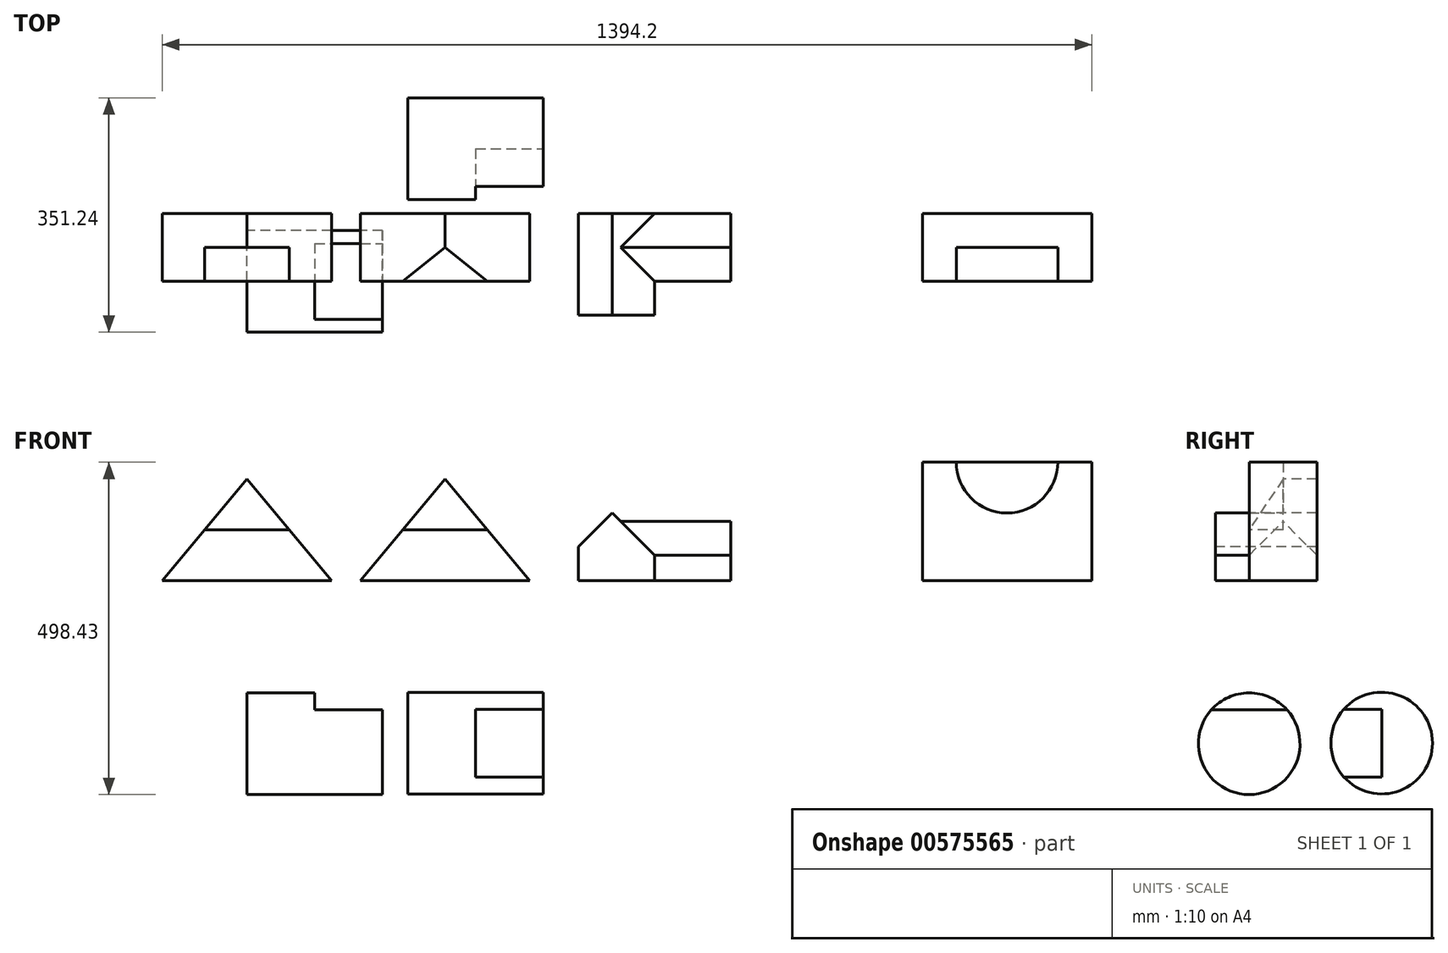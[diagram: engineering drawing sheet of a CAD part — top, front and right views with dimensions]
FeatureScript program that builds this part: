
annotation { "Feature Type Name" : "Feature", "Feature Type Description" : "" }
export const myFeature = defineFeature(function(context is Context, id is Id, definition is map)
    precondition{}
    {
        {
            var Q0;
            Q0=qCreatedBy(makeId("Front.planeOp"),FACE);
            var sketch = newSketch(context, id + "F0", { "sketchPlane" : qUnion([Q0])});
            skLineSegment(sketch, "E0", {"start": v(0, 0) * mm, "end": v(-127, 0) * mm});
            skLineSegment(sketch, "E1", {"start": v(-127, 0) * mm, "end": v(0, 152.4) * mm});
            skLineSegment(sketch, "E2", {"start": v(0, 0) * mm, "end": v(127, 0) * mm});
            skLineSegment(sketch, "E3", {"start": v(127, 0) * mm, "end": v(0, 152.4) * mm});
            skLineSegment(sketch, "E4", {"start": v(0, 76.2) * mm, "end": v(-63.5, 76.2) * mm});
            skLineSegment(sketch, "E5", {"start": v(0, 76.2) * mm, "end": v(63.5, 76.2) * mm});
            skSolve(sketch);
        }
        {
            var Q0;
            {var subQ3=sQuery(id+"F0.wireOp",EDGE,"E4");Q0=makeQuery(id+"F0.imprint","IMPRINT",FACE,{"disambiguationData":[TD([[makeQuery(id+"F0.imprint","IMPRINT",EDGE,{"derivedFrom":subQ3}),-1.0]])]});}
            var Q1;
            {var subQ4=sQuery(id+"F0.wireOp",EDGE,"E0");Q1=makeQuery(id+"F0.imprint","IMPRINT",FACE,{"disambiguationData":[TD([[makeQuery(id+"F0.imprint","IMPRINT",EDGE,{"derivedFrom":subQ4}),-1.0]])]});}
            extrude(context, id + "F1", {"entities" : qUnion([Q0, Q1]), "oppositeDirection" : true, "depth" : 101.6 * mm, "offsetDistance" : 25.4 * mm});
        }
        {
            var Q0;
            Q0=makeQuery(id+"F1.opExtrude","CAP_FACE",FACE,{"disambiguationData":[OSD([sQuery(id+"F0.wireOp",EDGE,"E0"),sQuery(id+"F0.wireOp",EDGE,"E1"),sQuery(id+"F0.wireOp",EDGE,"E2"),sQuery(id+"F0.wireOp",EDGE,"E3")])],"isStart":true});
            var sketch = newSketch(context, id + "F2", { "sketchPlane" : qUnion([Q0])});
            skLineSegment(sketch, "E6", {"start": v(0, 76.2) * mm, "end": v(-63.5, 76.2) * mm});
            skLineSegment(sketch, "E7", {"start": v(0, 76.2) * mm, "end": v(63.5, 76.2) * mm});
            skSolve(sketch);
        }
        {
            var Q0;
            {var subQ0=sQuery(id+"F2.wireOp",EDGE,"E6");Q0=makeQuery(id+"F2.imprint","IMPRINT",FACE,{"disambiguationData":[TD([[makeQuery(id+"F2.imprint","IMPRINT",EDGE,{"derivedFrom":subQ0}),-1.0]])]});}
            extrude(context, id + "F3", {"entities" : qUnion([Q0]), "operationType" : NewBodyOperationType.REMOVE, "oppositeDirection" : true, "depth" : 50.8 * mm, "offsetDistance" : 25.4 * mm});
        }
        {
            var Q0;
            Q0=qCreatedBy(makeId("Front.planeOp"),FACE);
            var sketch = newSketch(context, id + "F4", { "sketchPlane" : qUnion([Q0])});
            skLineSegment(sketch, "E8", {"start": v(170.18, 0) * mm, "end": v(424.18, 0) * mm});
            skLineSegment(sketch, "E9", {"start": v(297.18, 152.4) * mm, "end": v(170.18, 0) * mm});
            skLineSegment(sketch, "E10", {"start": v(297.18, 152.4) * mm, "end": v(424.18, 0) * mm});
            skLineSegment(sketch, "E11", {"start": v(297.18, 76.2) * mm, "end": v(233.68, 76.2) * mm});
            skLineSegment(sketch, "E12", {"start": v(297.18, 76.2) * mm, "end": v(360.68, 76.2) * mm});
            skSolve(sketch);
        }
        {
            var Q0;
            Q0 = qSketchRegion(id + "F4", true);
            extrude(context, id + "F5", {"entities" : qUnion([Q0]), "oppositeDirection" : true, "depth" : 101.6 * mm, "offsetDistance" : 25.4 * mm});
        }
        {
            var Q0;
            Q0=qCreatedBy(makeId("Front.planeOp"),FACE);
            var sketch = newSketch(context, id + "F6", { "sketchPlane" : qUnion([Q0])});
            skLineSegment(sketch, "E13", {"start": v(497, 0) * mm, "end": v(598.6, 0) * mm});
            skLineSegment(sketch, "E14", {"start": v(598.6, 0) * mm, "end": v(598.6, 50.8) * mm});
            skLineSegment(sketch, "E15", {"start": v(497, 0) * mm, "end": v(497, 50.8) * mm});
            skLineSegment(sketch, "E16", {"start": v(547.8, 101.6) * mm, "end": v(497, 50.8) * mm});
            skLineSegment(sketch, "E17", {"start": v(547.8, 101.6) * mm, "end": v(598.6, 50.8) * mm});
            skLineSegment(sketch, "E18", {"start": v(598.6, 0) * mm, "end": v(725.6, 0) * mm});
            skLineSegment(sketch, "E19", {"start": v(725.6, 0) * mm, "end": v(725.6, 50.8) * mm});
            skLineSegment(sketch, "E20", {"start": v(725.6, 50.8) * mm, "end": v(598.6, 50.8) * mm});
            skLineSegment(sketch, "E21", {"start": v(725.6, 50.8) * mm, "end": v(725.6, 88.9) * mm});
            skLineSegment(sketch, "E22", {"start": v(725.6, 88.9) * mm, "end": v(560.5, 88.9) * mm});
            skSolve(sketch);
        }
        {
            var Q0;
            Q0=makeQuery(id+"F6.imprint","IMPRINT",FACE,{"disambiguationData":[TD([[makeQuery(id+"F6.imprint","IMPRINT",EDGE,{"derivedFrom":sQuery(id+"F6.wireOp",EDGE,"E13")}),1.0]])]});
            var Q1;
            {var subQ0=sQuery(id+"F6.wireOp",EDGE,"E20");Q1=makeQuery(id+"F6.imprint","IMPRINT",FACE,{"disambiguationData":[TD([[makeQuery(id+"F6.imprint","IMPRINT",EDGE,{"derivedFrom":subQ0}),-1.0]])]});}
            var Q2;
            Q2=makeQuery(id+"F6.imprint","IMPRINT",FACE,{"disambiguationData":[TD([[makeQuery(id+"F6.imprint","IMPRINT",EDGE,{"derivedFrom":sQuery(id+"F6.wireOp",EDGE,"E14")}),-1.0]])]});
            extrude(context, id + "F7", {"entities" : qUnion([Q0, Q1, Q2]), "oppositeDirection" : true, "depth" : 101.6 * mm, "offsetDistance" : 25.4 * mm});
        }
        {
            var Q0;
            Q0=makeQuery(id+"F7.opExtrude","CAP_EDGE",EDGE,{"disambiguationData":[OSD([sQuery(id+"F6.wireOp",EDGE,"E22")])],"isStart":true});
            var Q1;
            Q1=makeQuery(id+"F7.opExtrude","CAP_EDGE",EDGE,{"disambiguationData":[OSD([sQuery(id+"F6.wireOp",EDGE,"E22")])],"isStart":false});
            chamfer(context, id + "F8", {"entities" : qUnion([Q0, Q1]), "width" : 50.8 * mm, "tangentPropagation" : true});
        }
        {
            var Q0;
            Q0=qCreatedBy(makeId("Front.planeOp"),FACE);
            var sketch = newSketch(context, id + "F9", { "sketchPlane" : qUnion([Q0])});
            skLineSegment(sketch, "E23", {"start": v(1013.2, 0) * mm, "end": v(1267.2, 0) * mm});
            skLineSegment(sketch, "E24", {"start": v(1267.2, 0) * mm, "end": v(1267.2, 177.8) * mm});
            skLineSegment(sketch, "E25", {"start": v(1267.2, 177.8) * mm, "end": v(1216.4, 177.8) * mm});
            skLineSegment(sketch, "E26", {"start": v(1013.2, 0) * mm, "end": v(1013.2, 177.8) * mm});
            skLineSegment(sketch, "E27", {"start": v(1013.2, 177.8) * mm, "end": v(1064, 177.8) * mm});
            skLineSegment(sketch, "E28", {"start": v(1064, 177.8) * mm, "end": v(1216.4, 177.8) * mm});
            skArc(sketch, "E29", {"start": v(1064, 177.8) * mm, "mid": v(1140.2, 101.6) * mm, "end": v(1216.4, 177.8) * mm});
            skSolve(sketch);
        }
        {
            var Q0;
            Q0=makeQuery(id+"F9.imprint","IMPRINT",FACE,{"disambiguationData":[TD([[makeQuery(id+"F9.imprint","IMPRINT",EDGE,{"derivedFrom":sQuery(id+"F9.wireOp",EDGE,"E23")}),1.0]])]});
            extrude(context, id + "F10", {"entities" : qUnion([Q0]), "oppositeDirection" : true, "depth" : 101.6 * mm, "offsetDistance" : 25.4 * mm});
        }
        {
            var Q0;
            Q0 = qSketchRegion(id + "F9", true);
            extrude(context, id + "F11", {"entities" : qUnion([Q0]), "operationType" : NewBodyOperationType.ADD, "oppositeDirection" : true, "depth" : 101.6 * mm, "offsetDistance" : 25.4 * mm});
        }
        {
            var Q0;
            Q0 = qSketchRegion(id + "F9", true);
            var Q1;
            {var subQ0=sQuery(id+"F9.wireOp",EDGE,"E27");var subQ1=sQuery(id+"F9.wireOp",EDGE,"E26");var subQ2=sQuery(id+"F9.wireOp",EDGE,"E25");var subQ3=sQuery(id+"F9.wireOp",EDGE,"E24");var subQ4=sQuery(id+"F9.wireOp",EDGE,"E23");Q1=makeQuery(id+"F11.boolean.opBoolean","MERGE",FACE,{"derivedFrom":[makeQuery(id+"F10.opExtrude","CAP_FACE",FACE,{"disambiguationData":[OSD([subQ4,subQ3,subQ2,subQ1,subQ0,sQuery(id+"F9.wireOp",EDGE,"E29")])],"isStart":true}),makeQuery(id+"F11.opExtrude","CAP_FACE",FACE,{"disambiguationData":[OSD([subQ4,subQ3,subQ2,subQ1,subQ0,sQuery(id+"F9.wireOp",EDGE,"E28")])],"isStart":true})]});}
            extrude(context, id + "F12", {"entities" : qUnion([Q0, Q1]), "operationType" : NewBodyOperationType.REMOVE, "oppositeDirection" : true, "depth" : 50.8 * mm, "offsetDistance" : 25.4 * mm});
        }
        {
            var Q0;
            Q0=makeQuery(id+"F12.boolean.opBoolean","COPY",FACE,{"derivedFrom":makeQuery(id+"F12.opExtrude","CAP_FACE",FACE,{"disambiguationData":[OSD([sQuery(id+"F9.wireOp",EDGE,"E23"),sQuery(id+"F9.wireOp",EDGE,"E24"),sQuery(id+"F9.wireOp",EDGE,"E25"),sQuery(id+"F9.wireOp",EDGE,"E26"),sQuery(id+"F9.wireOp",EDGE,"E27"),sQuery(id+"F9.wireOp",EDGE,"E28")])],"isStart":false})});
            var sketch = newSketch(context, id + "F13", { "sketchPlane" : qUnion([Q0])});
            skLineSegment(sketch, "E30", {"start": v(1013.2, 0) * mm, "end": v(1013.2, 177.8) * mm});
            skLineSegment(sketch, "E31", {"start": v(1013.2, 177.8) * mm, "end": v(1064, 177.8) * mm});
            skLineSegment(sketch, "E32", {"start": v(1013.2, 0) * mm, "end": v(1267.2, 0) * mm});
            skLineSegment(sketch, "E33", {"start": v(1267.2, 0) * mm, "end": v(1267.2, 177.8) * mm});
            skLineSegment(sketch, "E34", {"start": v(1267.2, 177.8) * mm, "end": v(1216.4, 177.8) * mm});
            skArc(sketch, "E35", {"start": v(1064, 177.8) * mm, "mid": v(1140.2, 101.6) * mm, "end": v(1216.4, 177.8) * mm});
            skSolve(sketch);
        }
        {
            var Q0;
            Q0 = qSketchRegion(id + "F13", true);
            var Q1;
            Q1=makeQuery(id+"F13.imprint","IMPRINT",FACE,{"disambiguationData":[TD([[makeQuery(id+"F13.imprint","IMPRINT",EDGE,{"derivedFrom":sQuery(id+"F13.wireOp",EDGE,"E30")}),-1.0]])]});
            extrude(context, id + "F14", {"entities" : qUnion([Q0, Q1]), "operationType" : NewBodyOperationType.ADD, "depth" : 50.8 * mm, "offsetDistance" : 25.4 * mm});
        }
        {
            var Q0;
            Q0=makeQuery(id+"F7.opExtrude","CAP_FACE",FACE,{"disambiguationData":[OSD([sQuery(id+"F6.wireOp",EDGE,"E13"),sQuery(id+"F6.wireOp",EDGE,"E15"),sQuery(id+"F6.wireOp",EDGE,"E16"),sQuery(id+"F6.wireOp",EDGE,"E17"),sQuery(id+"F6.wireOp",EDGE,"E18"),sQuery(id+"F6.wireOp",EDGE,"E19"),sQuery(id+"F6.wireOp",EDGE,"E21"),sQuery(id+"F6.wireOp",EDGE,"E22")])],"isStart":true});
            var sketch = newSketch(context, id + "F15", { "sketchPlane" : qUnion([Q0])});
            skLineSegment(sketch, "E36", {"start": v(611.3, 38.1) * mm, "end": v(611.3, 0) * mm});
            skSolve(sketch);
        }
        {
            var Q0;
            Q0 = qSketchRegion(id + "F15", true);
            var Q1;
            {var subQ1=sQuery(id+"F15.wireOp",EDGE,"E36");Q1=makeQuery(id+"F15.imprint","IMPRINT",FACE,{"disambiguationData":[TD([[makeQuery(id+"F15.imprint","IMPRINT",EDGE,{"derivedFrom":subQ1}),-1.0]])]});}
            extrude(context, id + "F16", {"entities" : qUnion([Q0, Q1]), "operationType" : NewBodyOperationType.ADD, "depth" : 50.8 * mm, "offsetDistance" : 25.4 * mm});
        }
        {
            var Q0;
            Q0=qCreatedBy(makeId("Right.planeOp"),FACE);
            var sketch = newSketch(context, id + "F17", { "sketchPlane" : qUnion([Q0])});
            skCircle(sketch, "E37", {"center": v(0, -244.43) * mm, "radius": 76.2 * mm});
            skSolve(sketch);
        }
        {
            var Q0;
            Q0=makeQuery(id+"F17.imprint","IMPRINT",FACE,{"disambiguationData":[TD([[makeQuery(id+"F17.imprint","IMPRINT",EDGE,{"derivedFrom":sQuery(id+"F17.wireOp",EDGE,"E37")}),1.0]])]});
            extrude(context, id + "F18", {"entities" : qUnion([Q0]), "depth" : 203.2 * mm, "offsetDistance" : 25.4 * mm});
        }
        {
            var Q0;
            Q0=makeQuery(id+"F18.opExtrude","CAP_FACE",FACE,{"disambiguationData":[OSD([sQuery(id+"F17.wireOp",EDGE,"E37")])],"isStart":false});
            var sketch = newSketch(context, id + "F19", { "sketchPlane" : qUnion([Q0])});
            skLineSegment(sketch, "E38", {"start": v(0, -193.63) * mm, "end": v(-56.8, -193.63) * mm});
            skLineSegment(sketch, "E39", {"start": v(0, -193.63) * mm, "end": v(56.8, -193.63) * mm});
            skSolve(sketch);
        }
        {
            var Q0;
            Q0 = qSketchRegion(id + "F19", true);
            var Q1;
            {var subQ0=sQuery(id+"F19.wireOp",EDGE,"E38");Q1=makeQuery(id+"F19.imprint","IMPRINT",FACE,{"disambiguationData":[TD([[makeQuery(id+"F19.imprint","IMPRINT",EDGE,{"derivedFrom":subQ0}),-1.0]])]});}
            extrude(context, id + "F20", {"entities" : qUnion([Q0, Q1]), "operationType" : NewBodyOperationType.REMOVE, "oppositeDirection" : true, "depth" : 101.6 * mm, "offsetDistance" : 25.4 * mm});
        }
        {
            var Q0;
            Q0=qCreatedBy(makeId("Right.planeOp"),FACE);
            cPlane(context, id + "F21", {"entities" : qUnion([Q0]), "cplaneType" : CPlaneType.OFFSET, "offset" : 241.3 * mm, "width" : 152.4 * mm, "height" : 152.4 * mm});
        }
        {
            var Q0;
            Q0=qCreatedBy(id+"F21.planeOp",FACE);
            var sketch = newSketch(context, id + "F22", { "sketchPlane" : qUnion([Q0])});
            skCircle(sketch, "E40", {"center": v(198.84, -243.5) * mm, "radius": 76.2 * mm});
            skLineSegment(sketch, "E41", {"start": v(198.84, -243.5) * mm, "end": v(198.84, -192.7) * mm});
            skLineSegment(sketch, "E42", {"start": v(198.84, -192.7) * mm, "end": v(142.04, -192.7) * mm});
            skLineSegment(sketch, "E43", {"start": v(198.84, -243.5) * mm, "end": v(198.84, -294.3) * mm});
            skLineSegment(sketch, "E44", {"start": v(198.84, -294.3) * mm, "end": v(142.04, -294.3) * mm});
            skSolve(sketch);
        }
        {
            var Q0;
            Q0=makeQuery(id+"F22.imprint","IMPRINT",FACE,{"disambiguationData":[TD([[makeQuery(id+"F22.imprint","IMPRINT",EDGE,{"derivedFrom":sQuery(id+"F22.wireOp",EDGE,"E41")}),1.0]])]});
            var Q1;
            Q1=makeQuery(id+"F22.imprint","IMPRINT",FACE,{"disambiguationData":[TD([[makeQuery(id+"F22.imprint","IMPRINT",EDGE,{"derivedFrom":sQuery(id+"F22.wireOp",EDGE,"E41")}),-1.0]])]});
            extrude(context, id + "F23", {"entities" : qUnion([Q0, Q1]), "depth" : 203.2 * mm, "offsetDistance" : 25.4 * mm});
        }
        {
            var Q0;
            Q0=makeQuery(id+"F23.opExtrude","CAP_FACE",FACE,{"disambiguationData":[OSD([sQuery(id+"F22.wireOp",EDGE,"E40")])],"isStart":false});
            var sketch = newSketch(context, id + "F24", { "sketchPlane" : qUnion([Q0])});
            skLineSegment(sketch, "E45", {"start": v(198.84, -243.5) * mm, "end": v(198.84, -192.7) * mm});
            skLineSegment(sketch, "E46", {"start": v(198.84, -192.7) * mm, "end": v(142.04, -192.7) * mm});
            skLineSegment(sketch, "E47", {"start": v(198.84, -243.5) * mm, "end": v(198.84, -294.3) * mm});
            skLineSegment(sketch, "E48", {"start": v(198.84, -294.3) * mm, "end": v(142.04, -294.3) * mm});
            skSolve(sketch);
        }
        {
            var Q0;
            Q0 = qSketchRegion(id + "F24", true);
            var Q1;
            Q1=makeQuery(id+"F24.imprint","IMPRINT",FACE,{"disambiguationData":[TD([[makeQuery(id+"F24.imprint","IMPRINT",EDGE,{"derivedFrom":sQuery(id+"F24.wireOp",EDGE,"E45")}),1.0]])]});
            extrude(context, id + "F25", {"entities" : qUnion([Q0, Q1]), "operationType" : NewBodyOperationType.REMOVE, "oppositeDirection" : true, "depth" : 101.6 * mm, "offsetDistance" : 25.4 * mm});
        }
        {
            var Q0;
            Q0=makeQuery(id+"F5.opExtrude","CAP_EDGE",EDGE,{"disambiguationData":[OSD([sQuery(id+"F4.wireOp",EDGE,"E8")])],"isStart":true});
            cPoint(context, id + "F26", {"entities" : qUnion([Q0]), "parameter" : 0.5});
        }
        {
            var Q0;
            Q0=makeQuery(id+"F5.opExtrude","CAP_VERTEX",VERTEX,{"disambiguationData":[OSD([sQuery(id+"F4.wireOp",EDGE,"E9"),sQuery(id+"F4.wireOp",EDGE,"E10")])],"isStart":true});
            var Q1;
            Q1=makeQuery(id+"F5.opExtrude","CAP_VERTEX",VERTEX,{"disambiguationData":[OSD([sQuery(id+"F4.wireOp",EDGE,"E9"),sQuery(id+"F4.wireOp",EDGE,"E10")])],"isStart":false});
            var Q2;
            Q2 = qCreatedBy(id + "F26" ,VERTEX);
            cPlane(context, id + "F27", {"entities" : qUnion([Q0, Q1, Q2]), "cplaneType" : CPlaneType.THREE_POINT, "offset" : 25.4 * mm, "width" : 152.4 * mm, "height" : 152.4 * mm});
        }
        {
            var Q0;
            Q0=qCreatedBy(id+"F27.planeOp",FACE);
            var sketch = newSketch(context, id + "F28", { "sketchPlane" : qUnion([Q0])});
            skLineSegment(sketch, "E49.0", {"start": v(0, 152.4) * mm, "end": v(0, 0) * mm});
            skLineSegment(sketch, "E50.0", {"start": v(101.6, 152.4) * mm, "end": v(0, 152.4) * mm});
            skLineSegment(sketch, "E51", {"start": v(0, 152.4) * mm, "end": v(50.8, 152.4) * mm});
            skLineSegment(sketch, "E52", {"start": v(0, 152.4) * mm, "end": v(0, 76.2) * mm});
            skLineSegment(sketch, "E53", {"start": v(0, 76.2) * mm, "end": v(50.8, 152.4) * mm});
            skSolve(sketch);
        }
        {
            var Q0;
            Q0 = qSketchRegion(id + "F28", true);
            extrude(context, id + "F29", {"entities" : qUnion([Q0]), "operationType" : NewBodyOperationType.REMOVE, "endBound" : BoundingType.SYMMETRIC, "oppositeDirection" : true, "depth" : 152.4 * mm, "offsetDistance" : 25.4 * mm});
        }
    });
